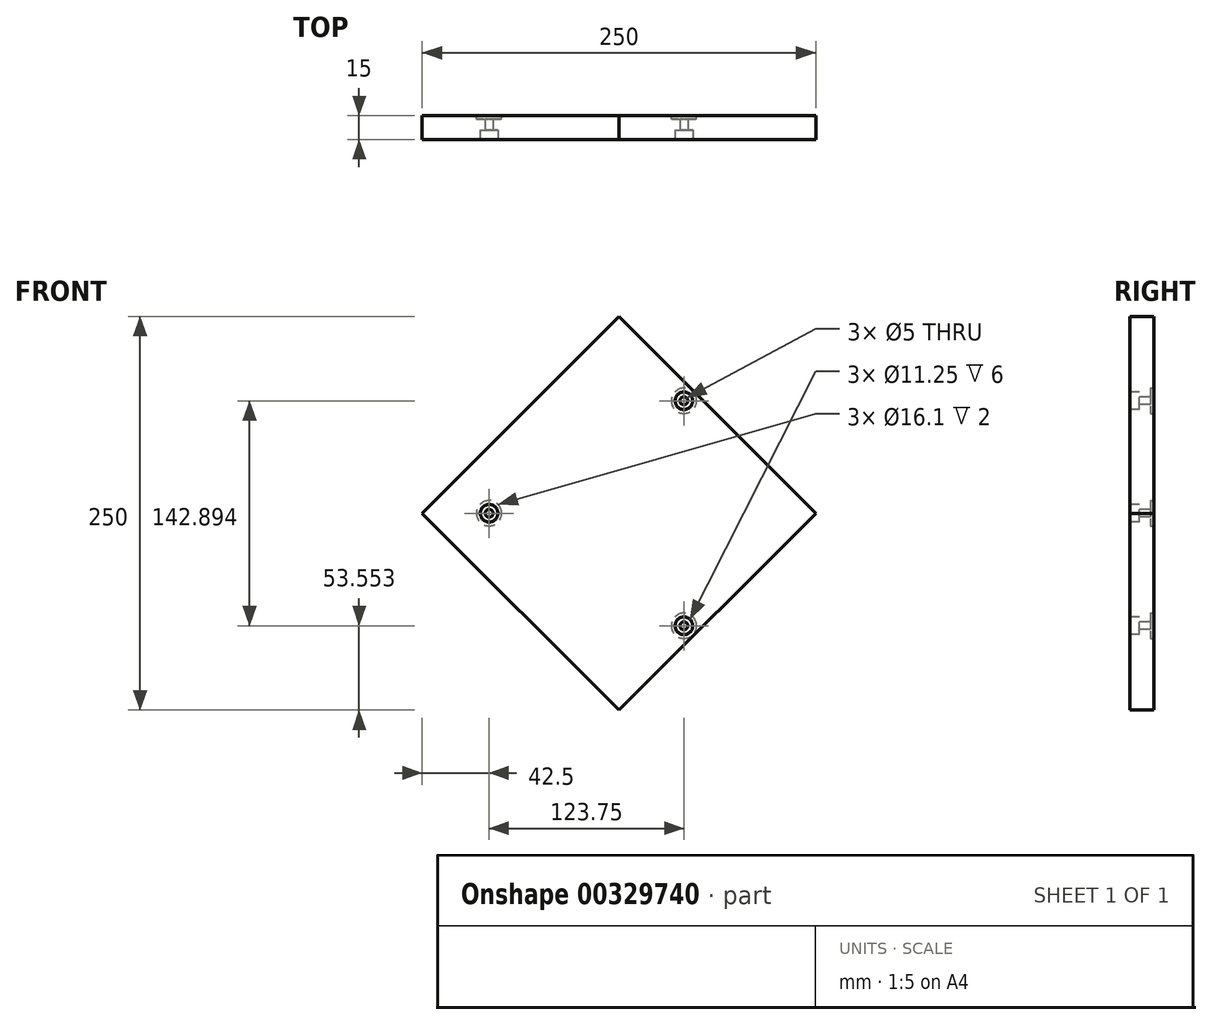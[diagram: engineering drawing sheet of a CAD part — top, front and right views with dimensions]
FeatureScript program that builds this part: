
annotation { "Feature Type Name" : "Feature", "Feature Type Description" : "" }
export const myFeature = defineFeature(function(context is Context, id is Id, definition is map)
    precondition{}
    {
        {
            var Q0;
            Q0=qCreatedBy(makeId("Front.planeOp"),FACE);
            var sketch = newSketch(context, id + "F0", { "sketchPlane" : qUnion([Q0])});
            skLineSegment(sketch, "E0", {"start": v(0, 111.82) * mm, "end": v(0, -93.68) * mm, "construction": true});
            skLineSegment(sketch, "E1", {"start": v(114.09, 0) * mm, "end": v(-79.4, 0) * mm, "construction": true});
            skLineSegment(sketch, "E2", {"start": v(0, 125) * mm, "end": v(-125, 0) * mm});
            skLineSegment(sketch, "E3", {"start": v(-125, 0) * mm, "end": v(0, -125) * mm});
            skLineSegment(sketch, "E4.MirrorCS", {"start": v(0, 125) * mm, "end": v(125, 0) * mm});
            skLineSegment(sketch, "E5.MirrorCS", {"start": v(125, 0) * mm, "end": v(0, -125) * mm});
            skSolve(sketch);
        }
        {
            var Q0;
            Q0=qSketchRegion(id+"F0",true);
            extrude(context, id + "F1", {"entities" : qUnion([Q0]), "depth" : 15 * mm});
        }
        {
            var Q0;
            Q0=makeQuery(id+"F1.opExtrude","CAP_FACE",FACE,{"disambiguationData":[OSD([sQuery(id+"F0.wireOp",EDGE,"E2"),sQuery(id+"F0.wireOp",EDGE,"E3"),sQuery(id+"F0.wireOp",EDGE,"E4.MirrorCS"),sQuery(id+"F0.wireOp",EDGE,"E5.MirrorCS")])],"isStart":false});
            var sketch = newSketch(context, id + "F2", { "sketchPlane" : qUnion([Q0])});
            skLineSegment(sketch, "E6", {"start": v(-125, 0) * mm, "end": v(135.73, 0) * mm, "construction": true});
            skLineSegment(sketch, "E7", {"start": v(0, 125) * mm, "end": v(0, -142.51) * mm, "construction": true});
            skCircle(sketch, "E8", {"center": v(0, 0) * mm, "radius": 82.5 * mm, "construction": true});
            skLineSegment(sketch, "E9", {"start": v(0, 0) * mm, "end": v(61.34, -106.25) * mm, "construction": true});
            skLineSegment(sketch, "E10", {"start": v(0, 0) * mm, "end": v(59.96, 103.86) * mm, "construction": true});
            skPoint(sketch, "E11", {"position": v(-82.5, 0) * mm});
            skPoint(sketch, "E12", {"position": v(41.25, 71.45) * mm});
            skPoint(sketch, "E13", {"position": v(41.25, -71.45) * mm});
            skCircle(sketch, "E14", {"center": v(-82.5, 0) * mm, "radius": 8.05 * mm});
            skCircle(sketch, "E15", {"center": v(41.25, -71.45) * mm, "radius": 8.05 * mm});
            skCircle(sketch, "E16", {"center": v(41.25, 71.45) * mm, "radius": 8.05 * mm});
            skSolve(sketch);
        }
        {
            var Q0;
            Q0=sQuery(id+"F2.wireOp",VERTEX,"E11");
            var Q1;
            Q1=sQuery(id+"F2.wireOp",VERTEX,"E13");
            var Q2;
            Q2=sQuery(id+"F2.wireOp",VERTEX,"E12");
            var Q3;
            Q3=makeQuery(id+"F1.opExtrude","SWEPT_BODY",BODY,{"disambiguationData":[OSD([sQuery(id+"F0.wireOp",EDGE,"E2"),sQuery(id+"F0.wireOp",EDGE,"E3"),sQuery(id+"F0.wireOp",EDGE,"E4.MirrorCS"),sQuery(id+"F0.wireOp",EDGE,"E5.MirrorCS")])]});
            hole(context, id + "F3", {"style" : HoleStyle.C_BORE, "endStyle" : HoleEndStyle.THROUGH, "standardTappedOrClearance" : lookupTablePath({ "standard" : "ISO", "engagement" : "75%", "pitch" : "1 mm", "size" : "M6", "type" : "Tapped" }), "standardBlindInLast" : lookupTablePath({ "standard" : "ISO", "engagement" : "75%", "pitch" : "1 mm", "size" : "M6", "type" : "Tapped" }), "holeDiameter" : 5 * mm, "cBoreDiameter" : 11.25 * mm, "cBoreDepth" : 6 * mm, "showTappedDepth" : true, "tappedDepth" : 15 * mm, "tapClearance" : 1, "locations" : qUnion([Q0, Q1, Q2]), "scope" : qUnion([Q3]), "majorDiameter" : 6 * mm});
        }
        {
            var Q0;
            Q0=makeQuery(id+"F1.opExtrude","CAP_FACE",FACE,{"disambiguationData":[OSD([sQuery(id+"F0.wireOp",EDGE,"E2"),sQuery(id+"F0.wireOp",EDGE,"E3"),sQuery(id+"F0.wireOp",EDGE,"E4.MirrorCS"),sQuery(id+"F0.wireOp",EDGE,"E5.MirrorCS")])],"isStart":true});
            var sketch = newSketch(context, id + "F4", { "sketchPlane" : qUnion([Q0])});
            skCircle(sketch, "E17", {"center": v(82.5, 0) * mm, "radius": 8.05 * mm});
            skCircle(sketch, "E18", {"center": v(-41.25, -71.45) * mm, "radius": 8.05 * mm});
            skCircle(sketch, "E19", {"center": v(-41.25, 71.45) * mm, "radius": 8.05 * mm});
            skSolve(sketch);
        }
        {
            var Q0;
            Q0=qSketchRegion(id+"F4",true);
            extrude(context, id + "F5", {"entities" : qUnion([Q0]), "operationType" : NewBodyOperationType.REMOVE, "oppositeDirection" : true, "depth" : 2 * mm});
        }
    });
